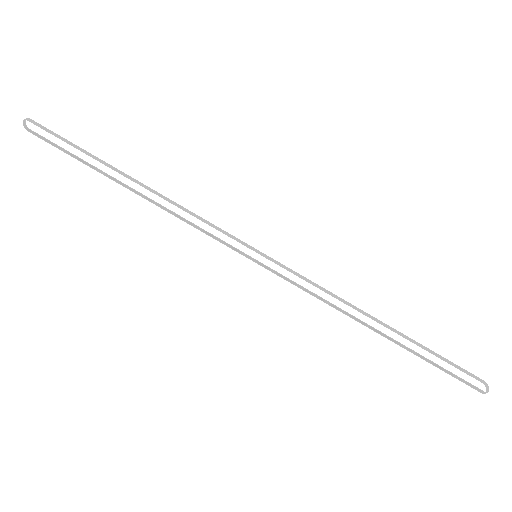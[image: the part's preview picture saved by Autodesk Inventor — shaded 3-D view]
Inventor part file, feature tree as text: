
AUTODESK INVENTOR PART (.ipt)
format: ipt  version: 2025.1 (Build 291241000, 241)  size: 11,249,664 bytes
history: native  units: mm
features: other x721, sketch x3, pattern_linear x2, extrude x2
ambient origin geometry x8: Origin, YZ Plane, XZ Plane, XY Plane, X Axis, Y Axis, Z Axis, Center Point
bodies: Body1 (feature_tree)
feature tree (728):
  other  "Bryła1"
  sketch  "Szkic1"
  other  "Punkt konstrukcyjny1"
  pattern_linear  "Szyk prostokątny1"  Spacing1=27.95mm  [1 undecoded]
  extrude  "Wyciągnięcie proste1"  Depth=1378.698mm
  pattern_linear  "Szyk prostokątny2"  Count1=720 Spacing1=10.0mm
  extrude  "Wyciągnięcie proste2"  Depth=1.0mm
  other  "Punkt konstrukcyjny2"
  other  "Punkt konstrukcyjny3"
  other  "Punkt konstrukcyjny4"
  other  "Punkt konstrukcyjny5"
  other  "Punkt konstrukcyjny6"
  other  "Punkt konstrukcyjny7"
  other  "Punkt konstrukcyjny8"
  other  "Punkt konstrukcyjny9"
  other  "Punkt konstrukcyjny10"
  other  "Punkt konstrukcyjny11"
  other  "Punkt konstrukcyjny12"
  other  "Punkt konstrukcyjny13"
  other  "Punkt konstrukcyjny14"
  other  "Punkt konstrukcyjny15"
  other  "Punkt konstrukcyjny16"
  other  "Punkt konstrukcyjny17"
  other  "Punkt konstrukcyjny18"
  other  "Punkt konstrukcyjny19"
  other  "Punkt konstrukcyjny20"
  other  "Punkt konstrukcyjny21"
  other  "Punkt konstrukcyjny22"
  other  "Punkt konstrukcyjny23"
  other  "Punkt konstrukcyjny24"
  other  "Punkt konstrukcyjny25"
  other  "Punkt konstrukcyjny26"
  other  "Punkt konstrukcyjny27"
  other  "Punkt konstrukcyjny28"
  other  "Punkt konstrukcyjny29"
  other  "Punkt konstrukcyjny30"
  other  "Punkt konstrukcyjny31"
  other  "Punkt konstrukcyjny32"
  other  "Punkt konstrukcyjny33"
  other  "Punkt konstrukcyjny34"
  other  "Punkt konstrukcyjny35"
  other  "Punkt konstrukcyjny36"
  other  "Punkt konstrukcyjny37"
  other  "Punkt konstrukcyjny38"
  other  "Punkt konstrukcyjny39"
  other  "Punkt konstrukcyjny40"
  other  "Punkt konstrukcyjny41"
  other  "Punkt konstrukcyjny42"
  other  "Punkt konstrukcyjny43"
  other  "Punkt konstrukcyjny44"
  other  "Punkt konstrukcyjny45"
  other  "Punkt konstrukcyjny46"
  other  "Punkt konstrukcyjny47"
  other  "Punkt konstrukcyjny48"
  other  "Punkt konstrukcyjny49"
  other  "Punkt konstrukcyjny50"
  other  "Punkt konstrukcyjny51"
  other  "Punkt konstrukcyjny52"
  other  "Punkt konstrukcyjny53"
  other  "Punkt konstrukcyjny54"
  other  "Punkt konstrukcyjny55"
  other  "Punkt konstrukcyjny56"
  other  "Punkt konstrukcyjny57"
  other  "Punkt konstrukcyjny58"
  other  "Punkt konstrukcyjny59"
  other  "Punkt konstrukcyjny60"
  other  "Punkt konstrukcyjny61"
  other  "Punkt konstrukcyjny62"
  other  "Punkt konstrukcyjny63"
  other  "Punkt konstrukcyjny64"
  other  "Punkt konstrukcyjny65"
  other  "Punkt konstrukcyjny66"
  other  "Punkt konstrukcyjny67"
  other  "Punkt konstrukcyjny68"
  other  "Punkt konstrukcyjny69"
  other  "Punkt konstrukcyjny70"
  other  "Punkt konstrukcyjny71"
  other  "Punkt konstrukcyjny72"
  other  "Punkt konstrukcyjny73"
  other  "Punkt konstrukcyjny74"
  other  "Punkt konstrukcyjny75"
  other  "Punkt konstrukcyjny76"
  other  "Punkt konstrukcyjny77"
  other  "Punkt konstrukcyjny78"
  other  "Punkt konstrukcyjny79"
  other  "Punkt konstrukcyjny80"
  other  "Punkt konstrukcyjny81"
  other  "Punkt konstrukcyjny82"
  other  "Punkt konstrukcyjny83"
  other  "Punkt konstrukcyjny84"
  other  "Punkt konstrukcyjny85"
  other  "Punkt konstrukcyjny86"
  other  "Punkt konstrukcyjny87"
  other  "Punkt konstrukcyjny88"
  other  "Punkt konstrukcyjny89"
  other  "Punkt konstrukcyjny90"
  other  "Punkt konstrukcyjny91"
  other  "Punkt konstrukcyjny92"
  other  "Punkt konstrukcyjny93"
  other  "Punkt konstrukcyjny94"
  other  "Punkt konstrukcyjny95"
  other  "Punkt konstrukcyjny96"
  other  "Punkt konstrukcyjny97"
  other  "Punkt konstrukcyjny98"
  other  "Punkt konstrukcyjny99"
  other  "Punkt konstrukcyjny100"
  other  "Punkt konstrukcyjny101"
  other  "Punkt konstrukcyjny102"
  other  "Punkt konstrukcyjny103"
  other  "Punkt konstrukcyjny104"
  other  "Punkt konstrukcyjny105"
  other  "Punkt konstrukcyjny106"
  other  "Punkt konstrukcyjny107"
  other  "Punkt konstrukcyjny108"
  other  "Punkt konstrukcyjny109"
  other  "Punkt konstrukcyjny110"
  other  "Punkt konstrukcyjny111"
  other  "Punkt konstrukcyjny112"
  other  "Punkt konstrukcyjny113"
  other  "Punkt konstrukcyjny114"
  other  "Punkt konstrukcyjny115"
  other  "Punkt konstrukcyjny116"
  other  "Punkt konstrukcyjny117"
  other  "Punkt konstrukcyjny118"
  other  "Punkt konstrukcyjny119"
  other  "Punkt konstrukcyjny120"
  other  "Punkt konstrukcyjny121"
  other  "Punkt konstrukcyjny122"
  other  "Punkt konstrukcyjny123"
  other  "Punkt konstrukcyjny124"
  other  "Punkt konstrukcyjny125"
  other  "Punkt konstrukcyjny126"
  other  "Punkt konstrukcyjny127"
  other  "Punkt konstrukcyjny128"
  other  "Punkt konstrukcyjny129"
  other  "Punkt konstrukcyjny130"
  other  "Punkt konstrukcyjny131"
  other  "Punkt konstrukcyjny132"
  other  "Punkt konstrukcyjny133"
  other  "Punkt konstrukcyjny134"
  other  "Punkt konstrukcyjny135"
  other  "Punkt konstrukcyjny136"
  other  "Punkt konstrukcyjny137"
  other  "Punkt konstrukcyjny138"
  other  "Punkt konstrukcyjny139"
  other  "Punkt konstrukcyjny140"
  other  "Punkt konstrukcyjny141"
  other  "Punkt konstrukcyjny142"
  other  "Punkt konstrukcyjny143"
  other  "Punkt konstrukcyjny144"
  other  "Punkt konstrukcyjny145"
  other  "Punkt konstrukcyjny146"
  other  "Punkt konstrukcyjny147"
  other  "Punkt konstrukcyjny148"
  other  "Punkt konstrukcyjny149"
  other  "Punkt konstrukcyjny150"
  other  "Punkt konstrukcyjny151"
  other  "Punkt konstrukcyjny152"
  other  "Punkt konstrukcyjny153"
  other  "Punkt konstrukcyjny154"
  other  "Punkt konstrukcyjny155"
  other  "Punkt konstrukcyjny156"
  other  "Punkt konstrukcyjny157"
  other  "Punkt konstrukcyjny158"
  other  "Punkt konstrukcyjny159"
  other  "Punkt konstrukcyjny160"
  other  "Punkt konstrukcyjny161"
  other  "Punkt konstrukcyjny162"
  other  "Punkt konstrukcyjny163"
  other  "Punkt konstrukcyjny164"
  other  "Punkt konstrukcyjny165"
  other  "Punkt konstrukcyjny166"
  other  "Punkt konstrukcyjny167"
  other  "Punkt konstrukcyjny168"
  other  "Punkt konstrukcyjny169"
  other  "Punkt konstrukcyjny170"
  other  "Punkt konstrukcyjny171"
  other  "Punkt konstrukcyjny172"
  other  "Punkt konstrukcyjny173"
  other  "Punkt konstrukcyjny174"
  other  "Punkt konstrukcyjny175"
  other  "Punkt konstrukcyjny176"
  other  "Punkt konstrukcyjny177"
  other  "Punkt konstrukcyjny178"
  other  "Punkt konstrukcyjny179"
  other  "Punkt konstrukcyjny180"
  other  "Punkt konstrukcyjny181"
  other  "Punkt konstrukcyjny182"
  other  "Punkt konstrukcyjny183"
  other  "Punkt konstrukcyjny184"
  other  "Punkt konstrukcyjny185"
  other  "Punkt konstrukcyjny186"
  other  "Punkt konstrukcyjny187"
  other  "Punkt konstrukcyjny188"
  other  "Punkt konstrukcyjny189"
  other  "Punkt konstrukcyjny190"
  other  "Punkt konstrukcyjny191"
  other  "Punkt konstrukcyjny192"
  other  "Punkt konstrukcyjny193"
  other  "Punkt konstrukcyjny194"
  other  "Punkt konstrukcyjny195"
  other  "Punkt konstrukcyjny196"
  other  "Punkt konstrukcyjny197"
  other  "Punkt konstrukcyjny198"
  other  "Punkt konstrukcyjny199"
  other  "Punkt konstrukcyjny200"
  other  "Punkt konstrukcyjny201"
  other  "Punkt konstrukcyjny202"
  other  "Punkt konstrukcyjny203"
  other  "Punkt konstrukcyjny204"
  other  "Punkt konstrukcyjny205"
  other  "Punkt konstrukcyjny206"
  other  "Punkt konstrukcyjny207"
  other  "Punkt konstrukcyjny208"
  other  "Punkt konstrukcyjny209"
  other  "Punkt konstrukcyjny210"
  other  "Punkt konstrukcyjny211"
  other  "Punkt konstrukcyjny212"
  other  "Punkt konstrukcyjny213"
  other  "Punkt konstrukcyjny214"
  other  "Punkt konstrukcyjny215"
  other  "Punkt konstrukcyjny216"
  other  "Punkt konstrukcyjny217"
  other  "Punkt konstrukcyjny218"
  other  "Punkt konstrukcyjny219"
  other  "Punkt konstrukcyjny220"
  other  "Punkt konstrukcyjny221"
  other  "Punkt konstrukcyjny222"
  other  "Punkt konstrukcyjny223"
  other  "Punkt konstrukcyjny224"
  other  "Punkt konstrukcyjny225"
  other  "Punkt konstrukcyjny226"
  other  "Punkt konstrukcyjny227"
  other  "Punkt konstrukcyjny228"
  other  "Punkt konstrukcyjny229"
  other  "Punkt konstrukcyjny230"
  other  "Punkt konstrukcyjny231"
  other  "Punkt konstrukcyjny232"
  other  "Punkt konstrukcyjny233"
  other  "Punkt konstrukcyjny234"
  other  "Punkt konstrukcyjny235"
  other  "Punkt konstrukcyjny236"
  other  "Punkt konstrukcyjny237"
  other  "Punkt konstrukcyjny238"
  other  "Punkt konstrukcyjny239"
  other  "Punkt konstrukcyjny240"
  other  "Punkt konstrukcyjny361"
  other  "Punkt konstrukcyjny362"
  other  "Punkt konstrukcyjny363"
  other  "Punkt konstrukcyjny364"
  other  "Punkt konstrukcyjny365"
  other  "Punkt konstrukcyjny366"
  other  "Punkt konstrukcyjny367"
  other  "Punkt konstrukcyjny368"
  other  "Punkt konstrukcyjny369"
  other  "Punkt konstrukcyjny370"
  other  "Punkt konstrukcyjny371"
  other  "Punkt konstrukcyjny372"
  other  "Punkt konstrukcyjny373"
  other  "Punkt konstrukcyjny374"
  other  "Punkt konstrukcyjny375"
  other  "Punkt konstrukcyjny376"
  other  "Punkt konstrukcyjny377"
  other  "Punkt konstrukcyjny378"
  other  "Punkt konstrukcyjny379"
  other  "Punkt konstrukcyjny380"
  other  "Punkt konstrukcyjny381"
  other  "Punkt konstrukcyjny382"
  other  "Punkt konstrukcyjny383"
  other  "Punkt konstrukcyjny384"
  other  "Punkt konstrukcyjny385"
  other  "Punkt konstrukcyjny386"
  other  "Punkt konstrukcyjny387"
  other  "Punkt konstrukcyjny388"
  other  "Punkt konstrukcyjny389"
  other  "Punkt konstrukcyjny390"
  other  "Punkt konstrukcyjny391"
  other  "Punkt konstrukcyjny392"
  other  "Punkt konstrukcyjny393"
  other  "Punkt konstrukcyjny394"
  other  "Punkt konstrukcyjny395"
  other  "Punkt konstrukcyjny396"
  other  "Punkt konstrukcyjny397"
  other  "Punkt konstrukcyjny398"
  other  "Punkt konstrukcyjny399"
  other  "Punkt konstrukcyjny400"
  other  "Punkt konstrukcyjny401"
  other  "Punkt konstrukcyjny402"
  other  "Punkt konstrukcyjny403"
  other  "Punkt konstrukcyjny404"
  other  "Punkt konstrukcyjny405"
  other  "Punkt konstrukcyjny406"
  other  "Punkt konstrukcyjny407"
  other  "Punkt konstrukcyjny408"
  other  "Punkt konstrukcyjny409"
  other  "Punkt konstrukcyjny410"
  other  "Punkt konstrukcyjny411"
  other  "Punkt konstrukcyjny412"
  other  "Punkt konstrukcyjny413"
  other  "Punkt konstrukcyjny414"
  other  "Punkt konstrukcyjny415"
  other  "Punkt konstrukcyjny416"
  other  "Punkt konstrukcyjny417"
  other  "Punkt konstrukcyjny418"
  other  "Punkt konstrukcyjny419"
  other  "Punkt konstrukcyjny420"
  other  "Punkt konstrukcyjny421"
  other  "Punkt konstrukcyjny422"
  other  "Punkt konstrukcyjny423"
  other  "Punkt konstrukcyjny424"
  other  "Punkt konstrukcyjny425"
  other  "Punkt konstrukcyjny426"
  other  "Punkt konstrukcyjny427"
  other  "Punkt konstrukcyjny428"
  other  "Punkt konstrukcyjny429"
  other  "Punkt konstrukcyjny430"
  other  "Punkt konstrukcyjny431"
  other  "Punkt konstrukcyjny432"
  other  "Punkt konstrukcyjny433"
  other  "Punkt konstrukcyjny434"
  other  "Punkt konstrukcyjny435"
  other  "Punkt konstrukcyjny436"
  other  "Punkt konstrukcyjny437"
  other  "Punkt konstrukcyjny438"
  other  "Punkt konstrukcyjny439"
  other  "Punkt konstrukcyjny440"
  other  "Punkt konstrukcyjny441"
  other  "Punkt konstrukcyjny442"
  other  "Punkt konstrukcyjny443"
  other  "Punkt konstrukcyjny444"
  other  "Punkt konstrukcyjny445"
  other  "Punkt konstrukcyjny446"
  other  "Punkt konstrukcyjny447"
  other  "Punkt konstrukcyjny448"
  other  "Punkt konstrukcyjny449"
  other  "Punkt konstrukcyjny450"
  other  "Punkt konstrukcyjny451"
  other  "Punkt konstrukcyjny452"
  other  "Punkt konstrukcyjny453"
  other  "Punkt konstrukcyjny454"
  other  "Punkt konstrukcyjny455"
  other  "Punkt konstrukcyjny456"
  other  "Punkt konstrukcyjny457"
  other  "Punkt konstrukcyjny458"
  other  "Punkt konstrukcyjny459"
  other  "Punkt konstrukcyjny460"
  other  "Punkt konstrukcyjny461"
  other  "Punkt konstrukcyjny462"
  other  "Punkt konstrukcyjny463"
  other  "Punkt konstrukcyjny464"
  other  "Punkt konstrukcyjny465"
  other  "Punkt konstrukcyjny466"
  other  "Punkt konstrukcyjny467"
  other  "Punkt konstrukcyjny468"
  other  "Punkt konstrukcyjny469"
  other  "Punkt konstrukcyjny470"
  other  "Punkt konstrukcyjny471"
  other  "Punkt konstrukcyjny472"
  other  "Punkt konstrukcyjny473"
  other  "Punkt konstrukcyjny474"
  other  "Punkt konstrukcyjny475"
  other  "Punkt konstrukcyjny476"
  other  "Punkt konstrukcyjny477"
  other  "Punkt konstrukcyjny478"
  other  "Punkt konstrukcyjny479"
  other  "Punkt konstrukcyjny480"
  other  "Punkt konstrukcyjny481"
  other  "Punkt konstrukcyjny482"
  other  "Punkt konstrukcyjny483"
  other  "Punkt konstrukcyjny484"
  other  "Punkt konstrukcyjny485"
  other  "Punkt konstrukcyjny486"
  other  "Punkt konstrukcyjny487"
  other  "Punkt konstrukcyjny488"
  other  "Punkt konstrukcyjny489"
  other  "Punkt konstrukcyjny490"
  other  "Punkt konstrukcyjny491"
  other  "Punkt konstrukcyjny492"
  other  "Punkt konstrukcyjny493"
  other  "Punkt konstrukcyjny494"
  other  "Punkt konstrukcyjny495"
  other  "Punkt konstrukcyjny496"
  other  "Punkt konstrukcyjny497"
  other  "Punkt konstrukcyjny498"
  other  "Punkt konstrukcyjny499"
  other  "Punkt konstrukcyjny500"
  other  "Punkt konstrukcyjny501"
  other  "Punkt konstrukcyjny502"
  other  "Punkt konstrukcyjny503"
  other  "Punkt konstrukcyjny504"
  other  "Punkt konstrukcyjny505"
  other  "Punkt konstrukcyjny506"
  other  "Punkt konstrukcyjny507"
  other  "Punkt konstrukcyjny508"
  other  "Punkt konstrukcyjny509"
  other  "Punkt konstrukcyjny510"
  other  "Punkt konstrukcyjny511"
  other  "Punkt konstrukcyjny512"
  other  "Punkt konstrukcyjny513"
  other  "Punkt konstrukcyjny514"
  other  "Punkt konstrukcyjny515"
  other  "Punkt konstrukcyjny516"
  other  "Punkt konstrukcyjny517"
  other  "Punkt konstrukcyjny518"
  other  "Punkt konstrukcyjny519"
  other  "Punkt konstrukcyjny520"
  other  "Punkt konstrukcyjny521"
  other  "Punkt konstrukcyjny522"
  other  "Punkt konstrukcyjny523"
  other  "Punkt konstrukcyjny524"
  other  "Punkt konstrukcyjny525"
  other  "Punkt konstrukcyjny526"
  other  "Punkt konstrukcyjny527"
  other  "Punkt konstrukcyjny528"
  other  "Punkt konstrukcyjny529"
  other  "Punkt konstrukcyjny530"
  other  "Punkt konstrukcyjny531"
  other  "Punkt konstrukcyjny532"
  other  "Punkt konstrukcyjny533"
  other  "Punkt konstrukcyjny534"
  other  "Punkt konstrukcyjny535"
  other  "Punkt konstrukcyjny536"
  other  "Punkt konstrukcyjny537"
  other  "Punkt konstrukcyjny538"
  other  "Punkt konstrukcyjny539"
  other  "Punkt konstrukcyjny540"
  other  "Punkt konstrukcyjny541"
  other  "Punkt konstrukcyjny542"
  other  "Punkt konstrukcyjny543"
  other  "Punkt konstrukcyjny544"
  other  "Punkt konstrukcyjny545"
  other  "Punkt konstrukcyjny546"
  other  "Punkt konstrukcyjny547"
  other  "Punkt konstrukcyjny548"
  other  "Punkt konstrukcyjny549"
  other  "Punkt konstrukcyjny550"
  other  "Punkt konstrukcyjny551"
  other  "Punkt konstrukcyjny552"
  other  "Punkt konstrukcyjny553"
  other  "Punkt konstrukcyjny554"
  other  "Punkt konstrukcyjny555"
  other  "Punkt konstrukcyjny556"
  other  "Punkt konstrukcyjny557"
  other  "Punkt konstrukcyjny558"
  other  "Punkt konstrukcyjny559"
  other  "Punkt konstrukcyjny560"
  other  "Punkt konstrukcyjny561"
  other  "Punkt konstrukcyjny562"
  other  "Punkt konstrukcyjny563"
  other  "Punkt konstrukcyjny564"
  other  "Punkt konstrukcyjny565"
  other  "Punkt konstrukcyjny566"
  other  "Punkt konstrukcyjny567"
  other  "Punkt konstrukcyjny568"
  other  "Punkt konstrukcyjny569"
  other  "Punkt konstrukcyjny570"
  other  "Punkt konstrukcyjny571"
  other  "Punkt konstrukcyjny572"
  other  "Punkt konstrukcyjny573"
  other  "Punkt konstrukcyjny574"
  other  "Punkt konstrukcyjny575"
  other  "Punkt konstrukcyjny576"
  other  "Punkt konstrukcyjny577"
  other  "Punkt konstrukcyjny578"
  other  "Punkt konstrukcyjny579"
  other  "Punkt konstrukcyjny580"
  other  "Punkt konstrukcyjny581"
  other  "Punkt konstrukcyjny582"
  other  "Punkt konstrukcyjny583"
  other  "Punkt konstrukcyjny584"
  other  "Punkt konstrukcyjny585"
  other  "Punkt konstrukcyjny586"
  other  "Punkt konstrukcyjny587"
  other  "Punkt konstrukcyjny588"
  other  "Punkt konstrukcyjny589"
  other  "Punkt konstrukcyjny590"
  other  "Punkt konstrukcyjny591"
  other  "Punkt konstrukcyjny592"
  other  "Punkt konstrukcyjny593"
  other  "Punkt konstrukcyjny594"
  other  "Punkt konstrukcyjny595"
  other  "Punkt konstrukcyjny596"
  other  "Punkt konstrukcyjny597"
  other  "Punkt konstrukcyjny598"
  other  "Punkt konstrukcyjny599"
  other  "Punkt konstrukcyjny600"
  other  "Punkt konstrukcyjny601"
  other  "Punkt konstrukcyjny602"
  other  "Punkt konstrukcyjny603"
  other  "Punkt konstrukcyjny604"
  other  "Punkt konstrukcyjny605"
  other  "Punkt konstrukcyjny606"
  other  "Punkt konstrukcyjny607"
  other  "Punkt konstrukcyjny608"
  other  "Punkt konstrukcyjny609"
  other  "Punkt konstrukcyjny610"
  other  "Punkt konstrukcyjny611"
  other  "Punkt konstrukcyjny612"
  other  "Punkt konstrukcyjny613"
  other  "Punkt konstrukcyjny614"
  other  "Punkt konstrukcyjny615"
  other  "Punkt konstrukcyjny616"
  other  "Punkt konstrukcyjny617"
  other  "Punkt konstrukcyjny618"
  other  "Punkt konstrukcyjny619"
  other  "Punkt konstrukcyjny620"
  other  "Punkt konstrukcyjny621"
  other  "Punkt konstrukcyjny622"
  other  "Punkt konstrukcyjny623"
  other  "Punkt konstrukcyjny624"
  other  "Punkt konstrukcyjny625"
  other  "Punkt konstrukcyjny626"
  other  "Punkt konstrukcyjny627"
  other  "Punkt konstrukcyjny628"
  other  "Punkt konstrukcyjny629"
  other  "Punkt konstrukcyjny630"
  other  "Punkt konstrukcyjny631"
  other  "Punkt konstrukcyjny632"
  other  "Punkt konstrukcyjny633"
  other  "Punkt konstrukcyjny634"
  other  "Punkt konstrukcyjny635"
  other  "Punkt konstrukcyjny636"
  other  "Punkt konstrukcyjny637"
  other  "Punkt konstrukcyjny638"
  other  "Punkt konstrukcyjny639"
  other  "Punkt konstrukcyjny640"
  other  "Punkt konstrukcyjny641"
  other  "Punkt konstrukcyjny642"
  other  "Punkt konstrukcyjny643"
  other  "Punkt konstrukcyjny644"
  other  "Punkt konstrukcyjny645"
  other  "Punkt konstrukcyjny646"
  other  "Punkt konstrukcyjny647"
  other  "Punkt konstrukcyjny648"
  other  "Punkt konstrukcyjny649"
  other  "Punkt konstrukcyjny650"
  other  "Punkt konstrukcyjny651"
  other  "Punkt konstrukcyjny652"
  other  "Punkt konstrukcyjny653"
  other  "Punkt konstrukcyjny654"
  other  "Punkt konstrukcyjny655"
  other  "Punkt konstrukcyjny656"
  other  "Punkt konstrukcyjny657"
  other  "Punkt konstrukcyjny658"
  other  "Punkt konstrukcyjny659"
  other  "Punkt konstrukcyjny660"
  other  "Punkt konstrukcyjny661"
  other  "Punkt konstrukcyjny662"
  other  "Punkt konstrukcyjny663"
  other  "Punkt konstrukcyjny664"
  other  "Punkt konstrukcyjny665"
  other  "Punkt konstrukcyjny666"
  other  "Punkt konstrukcyjny667"
  other  "Punkt konstrukcyjny668"
  other  "Punkt konstrukcyjny669"
  other  "Punkt konstrukcyjny670"
  other  "Punkt konstrukcyjny671"
  other  "Punkt konstrukcyjny672"
  other  "Punkt konstrukcyjny673"
  other  "Punkt konstrukcyjny674"
  other  "Punkt konstrukcyjny675"
  other  "Punkt konstrukcyjny676"
  other  "Punkt konstrukcyjny677"
  other  "Punkt konstrukcyjny678"
  other  "Punkt konstrukcyjny679"
  other  "Punkt konstrukcyjny680"
  other  "Punkt konstrukcyjny681"
  other  "Punkt konstrukcyjny682"
  other  "Punkt konstrukcyjny683"
  other  "Punkt konstrukcyjny684"
  other  "Punkt konstrukcyjny685"
  other  "Punkt konstrukcyjny686"
  other  "Punkt konstrukcyjny687"
  other  "Punkt konstrukcyjny688"
  other  "Punkt konstrukcyjny689"
  other  "Punkt konstrukcyjny690"
  other  "Punkt konstrukcyjny691"
  other  "Punkt konstrukcyjny692"
  other  "Punkt konstrukcyjny693"
  other  "Punkt konstrukcyjny694"
  other  "Punkt konstrukcyjny695"
  other  "Punkt konstrukcyjny696"
  other  "Punkt konstrukcyjny697"
  other  "Punkt konstrukcyjny698"
  other  "Punkt konstrukcyjny699"
  other  "Punkt konstrukcyjny700"
  other  "Punkt konstrukcyjny701"
  other  "Punkt konstrukcyjny702"
  other  "Punkt konstrukcyjny703"
  other  "Punkt konstrukcyjny704"
  other  "Punkt konstrukcyjny705"
  other  "Punkt konstrukcyjny706"
  other  "Punkt konstrukcyjny707"
  other  "Punkt konstrukcyjny708"
  other  "Punkt konstrukcyjny709"
  other  "Punkt konstrukcyjny710"
  other  "Punkt konstrukcyjny711"
  other  "Punkt konstrukcyjny712"
  other  "Punkt konstrukcyjny713"
  other  "Punkt konstrukcyjny714"
  other  "Punkt konstrukcyjny715"
  other  "Punkt konstrukcyjny716"
  other  "Punkt konstrukcyjny717"
  other  "Punkt konstrukcyjny718"
  other  "Punkt konstrukcyjny719"
  other  "Punkt konstrukcyjny720"
  other  "Punkt konstrukcyjny721"
  other  "Punkt konstrukcyjny722"
  other  "Punkt konstrukcyjny723"
  other  "Punkt konstrukcyjny724"
  other  "Punkt konstrukcyjny725"
  other  "Punkt konstrukcyjny726"
  other  "Punkt konstrukcyjny727"
  other  "Punkt konstrukcyjny728"
  other  "Punkt konstrukcyjny729"
  other  "Punkt konstrukcyjny730"
  other  "Punkt konstrukcyjny731"
  other  "Punkt konstrukcyjny732"
  other  "Punkt konstrukcyjny733"
  other  "Punkt konstrukcyjny734"
  other  "Punkt konstrukcyjny735"
  other  "Punkt konstrukcyjny736"
  other  "Punkt konstrukcyjny737"
  other  "Punkt konstrukcyjny738"
  other  "Punkt konstrukcyjny739"
  other  "Punkt konstrukcyjny740"
  other  "Punkt konstrukcyjny741"
  other  "Punkt konstrukcyjny742"
  other  "Punkt konstrukcyjny743"
  other  "Punkt konstrukcyjny744"
  other  "Punkt konstrukcyjny745"
  other  "Punkt konstrukcyjny746"
  other  "Punkt konstrukcyjny747"
  other  "Punkt konstrukcyjny748"
  other  "Punkt konstrukcyjny749"
  other  "Punkt konstrukcyjny750"
  other  "Punkt konstrukcyjny751"
  other  "Punkt konstrukcyjny752"
  other  "Punkt konstrukcyjny753"
  other  "Punkt konstrukcyjny754"
  other  "Punkt konstrukcyjny755"
  other  "Punkt konstrukcyjny756"
  other  "Punkt konstrukcyjny757"
  other  "Punkt konstrukcyjny758"
  other  "Punkt konstrukcyjny759"
  other  "Punkt konstrukcyjny760"
  other  "Punkt konstrukcyjny761"
  other  "Punkt konstrukcyjny762"
  other  "Punkt konstrukcyjny763"
  other  "Punkt konstrukcyjny764"
  other  "Punkt konstrukcyjny765"
  other  "Punkt konstrukcyjny766"
  other  "Punkt konstrukcyjny767"
  other  "Punkt konstrukcyjny768"
  other  "Punkt konstrukcyjny769"
  other  "Punkt konstrukcyjny770"
  other  "Punkt konstrukcyjny771"
  other  "Punkt konstrukcyjny772"
  other  "Punkt konstrukcyjny773"
  other  "Punkt konstrukcyjny774"
  other  "Punkt konstrukcyjny775"
  other  "Punkt konstrukcyjny776"
  other  "Punkt konstrukcyjny777"
  other  "Punkt konstrukcyjny778"
  other  "Punkt konstrukcyjny779"
  other  "Punkt konstrukcyjny780"
  other  "Punkt konstrukcyjny781"
  other  "Punkt konstrukcyjny782"
  other  "Punkt konstrukcyjny783"
  other  "Punkt konstrukcyjny784"
  other  "Punkt konstrukcyjny785"
  other  "Punkt konstrukcyjny786"
  other  "Punkt konstrukcyjny787"
  other  "Punkt konstrukcyjny788"
  other  "Punkt konstrukcyjny789"
  other  "Punkt konstrukcyjny790"
  other  "Punkt konstrukcyjny791"
  other  "Punkt konstrukcyjny792"
  other  "Punkt konstrukcyjny793"
  other  "Punkt konstrukcyjny794"
  other  "Punkt konstrukcyjny795"
  other  "Punkt konstrukcyjny796"
  other  "Punkt konstrukcyjny797"
  other  "Punkt konstrukcyjny798"
  other  "Punkt konstrukcyjny799"
  other  "Punkt konstrukcyjny800"
  other  "Punkt konstrukcyjny801"
  other  "Punkt konstrukcyjny802"
  other  "Punkt konstrukcyjny803"
  other  "Punkt konstrukcyjny804"
  other  "Punkt konstrukcyjny805"
  other  "Punkt konstrukcyjny806"
  other  "Punkt konstrukcyjny807"
  other  "Punkt konstrukcyjny808"
  other  "Punkt konstrukcyjny809"
  other  "Punkt konstrukcyjny810"
  other  "Punkt konstrukcyjny811"
  other  "Punkt konstrukcyjny812"
  other  "Punkt konstrukcyjny813"
  other  "Punkt konstrukcyjny814"
  other  "Punkt konstrukcyjny815"
  other  "Punkt konstrukcyjny816"
  other  "Punkt konstrukcyjny817"
  other  "Punkt konstrukcyjny818"
  other  "Punkt konstrukcyjny819"
  other  "Punkt konstrukcyjny820"
  other  "Punkt konstrukcyjny821"
  other  "Punkt konstrukcyjny822"
  other  "Punkt konstrukcyjny823"
  other  "Punkt konstrukcyjny824"
  other  "Punkt konstrukcyjny825"
  other  "Punkt konstrukcyjny826"
  other  "Punkt konstrukcyjny827"
  other  "Punkt konstrukcyjny828"
  other  "Punkt konstrukcyjny829"
  other  "Punkt konstrukcyjny830"
  other  "Punkt konstrukcyjny831"
  other  "Punkt konstrukcyjny832"
  other  "Punkt konstrukcyjny833"
  other  "Punkt konstrukcyjny834"
  other  "Punkt konstrukcyjny835"
  other  "Punkt konstrukcyjny836"
  other  "Punkt konstrukcyjny837"
  other  "Punkt konstrukcyjny838"
  other  "Punkt konstrukcyjny839"
  other  "Punkt konstrukcyjny840"
  sketch  "Szkic4"
  sketch  "Szkic5"
note: 1 required parameter value undecoded (feature->parameter linkage not recoverable at this tier; creation-order binding heuristic only, values carry confidence <= 0.55)
